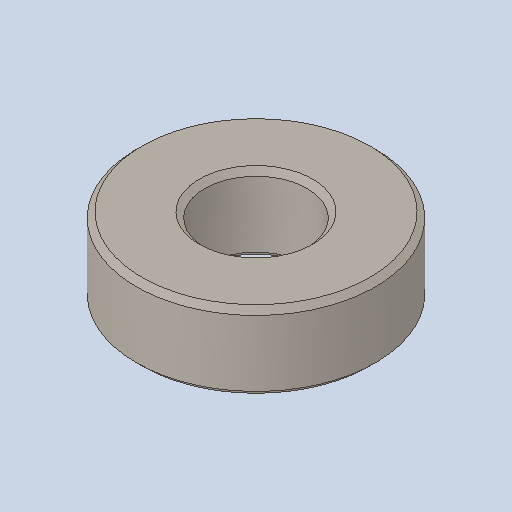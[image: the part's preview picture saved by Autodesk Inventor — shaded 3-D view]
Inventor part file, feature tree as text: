
AUTODESK INVENTOR PART (.ipt)
format: ipt  version: 2023.4 (Build 274418000, 418)  size: 104,448 bytes
history: native  units: in
note: dims shown in document units (in); Inventor stores cm internally (conversion verified against a paired STEP export)
features: chamfer x1
ambient origin geometry x8: Origin, YZ Plane, XZ Plane, XY Plane, X Axis, Y Axis, Z Axis, Center Point
bodies: Solid1 (feature_tree)
feature tree (1):
  chamfer  "Chamfer1"  [1 undecoded]
note: 1 required parameter value undecoded (feature->parameter linkage not recoverable at this tier; creation-order binding heuristic only, values carry confidence <= 0.55)
